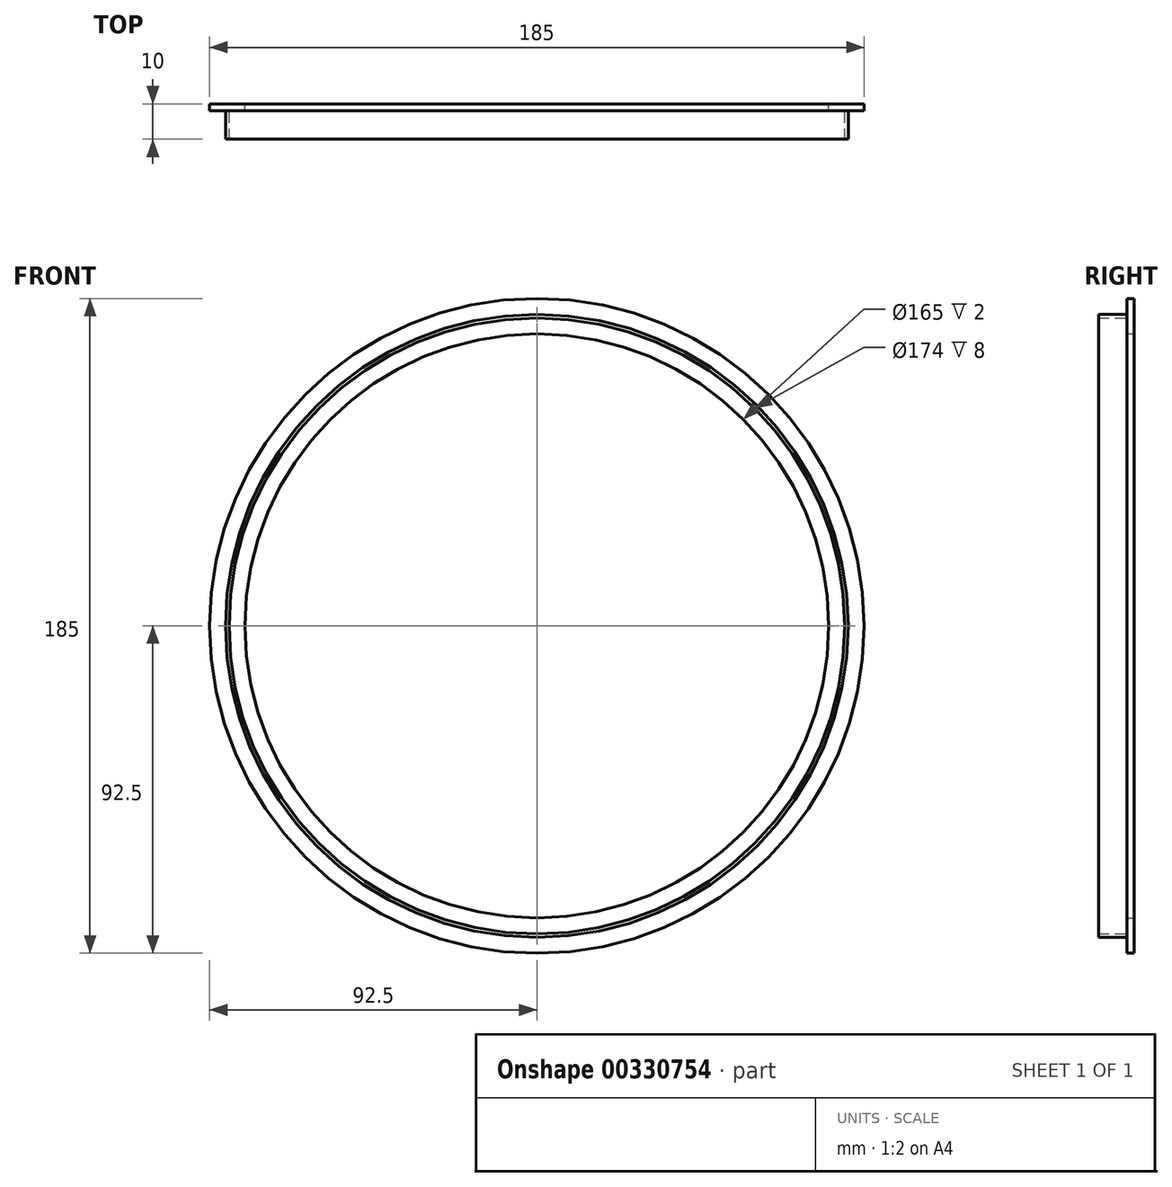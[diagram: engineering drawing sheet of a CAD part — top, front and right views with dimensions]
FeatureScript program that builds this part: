
annotation { "Feature Type Name" : "Feature", "Feature Type Description" : "" }
export const myFeature = defineFeature(function(context is Context, id is Id, definition is map)
    precondition{}
    {
        {
            var Q0;
            Q0=qCreatedBy(makeId("Front.planeOp"),FACE);
            var sketch = newSketch(context, id + "F0", { "sketchPlane" : qUnion([Q0])});
            skCircle(sketch, "E0", {"center": v(0, 0) * mm, "radius": 92.5 * mm});
            skCircle(sketch, "E1", {"center": v(0, 0) * mm, "radius": 82.5 * mm});
            skSolve(sketch);
        }
        {
            var Q0;
            Q0=makeQuery(id+"F0.imprint","IMPRINT",FACE,{"disambiguationData":[TD([[makeQuery(id+"F0.imprint","IMPRINT",EDGE,{"derivedFrom":sQuery(id+"F0.wireOp",EDGE,"E0")}),1.0]])]});
            extrude(context, id + "F1", {"entities" : qUnion([Q0]), "depth" : 2 * mm});
        }
        {
            var Q0;
            Q0=qCreatedBy(makeId("Front.planeOp"),FACE);
            var sketch = newSketch(context, id + "F2", { "sketchPlane" : qUnion([Q0])});
            skCircle(sketch, "E2", {"center": v(0, 0) * mm, "radius": 88 * mm});
            skCircle(sketch, "E3", {"center": v(0, 0) * mm, "radius": 87 * mm});
            skSolve(sketch);
        }
        {
            var Q0;
            Q0 = qSketchRegion(id + "F2", true);
            extrude(context, id + "F3", {"entities" : qUnion([Q0]), "operationType" : NewBodyOperationType.ADD, "depth" : 10 * mm});
        }
    });
